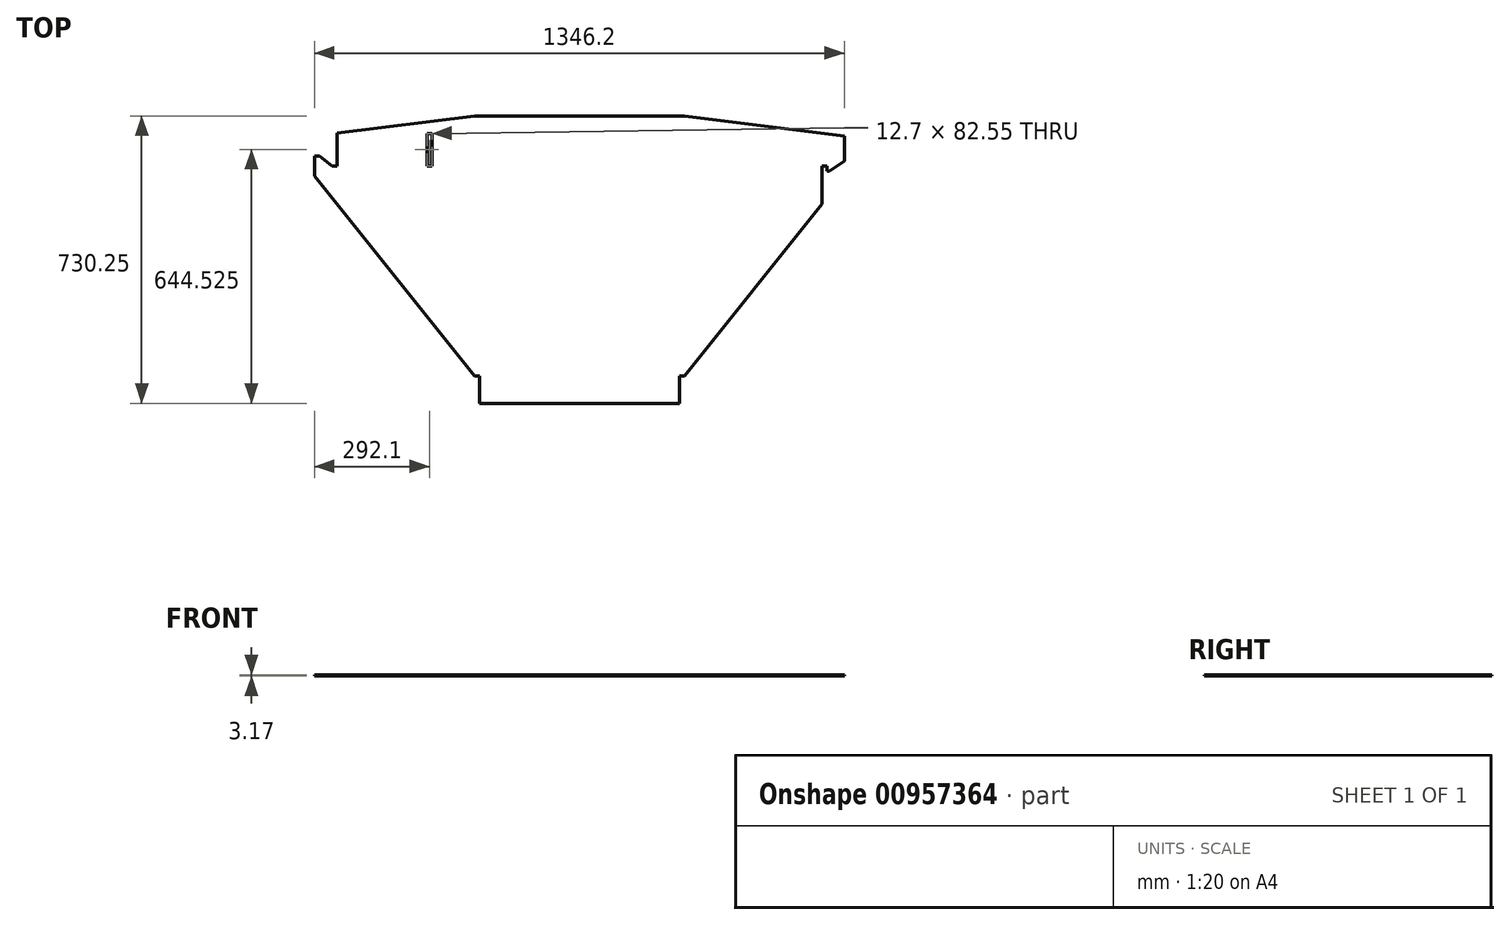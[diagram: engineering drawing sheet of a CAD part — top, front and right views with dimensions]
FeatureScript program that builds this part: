
annotation { "Feature Type Name" : "Feature", "Feature Type Description" : "" }
export const myFeature = defineFeature(function(context is Context, id is Id, definition is map)
    precondition{}
    {
        {
            var Q0;
            Q0=qCreatedBy(makeId("Top.planeOp"),FACE);
            var sketch = newSketch(context, id + "F0", { "sketchPlane" : qUnion([Q0])});
            skLineSegment(sketch, "E0.bottom", {"start": v(0, -660.4) * mm, "end": v(508, -660.4) * mm});
            skLineSegment(sketch, "E0.top", {"start": v(0, 0) * mm, "end": v(508, 0) * mm});
            skLineSegment(sketch, "E0.left", {"start": v(0, -660.4) * mm, "end": v(0, 0) * mm});
            skLineSegment(sketch, "E0.right", {"start": v(508, -660.4) * mm, "end": v(508, 0) * mm});
            skLineSegment(sketch, "E1.bottom", {"start": v(508, -660.4) * mm, "end": v(520.7, -660.4) * mm});
            skLineSegment(sketch, "E1.top", {"start": v(508, 0) * mm, "end": v(520.7, 0) * mm});
            skLineSegment(sketch, "E1.right", {"start": v(520.7, -660.4) * mm, "end": v(520.7, 0) * mm});
            skLineSegment(sketch, "E2", {"start": v(927.1, -50.8) * mm, "end": v(927.1, -114.3) * mm});
            skLineSegment(sketch, "E3", {"start": v(882.65, -139.7) * mm, "end": v(882.65, -127) * mm});
            skLineSegment(sketch, "E4", {"start": v(882.65, -127) * mm, "end": v(869.95, -127) * mm});
            skLineSegment(sketch, "E5", {"start": v(869.95, -127) * mm, "end": v(869.95, -223.84) * mm});
            skLineSegment(sketch, "E6", {"start": v(869.95, -223.84) * mm, "end": v(520.7, -660.4) * mm});
            skLineSegment(sketch, "E7", {"start": v(520.7, 0) * mm, "end": v(927.1, -50.8) * mm});
            skLineSegment(sketch, "E8", {"start": v(869.95, -223.84) * mm, "end": v(927.1, -152.4) * mm, "construction": true});
            skLineSegment(sketch, "E9", {"start": v(882.65, -139.7) * mm, "end": v(889, -139.7) * mm});
            skLineSegment(sketch, "E10", {"start": v(889, -139.7) * mm, "end": v(927.1, -114.3) * mm});
            skLineSegment(sketch, "E11.bottom", {"start": v(0, -660.4) * mm, "end": v(-12.7, -660.4) * mm});
            skLineSegment(sketch, "E11.top", {"start": v(0, 0) * mm, "end": v(-12.7, 0) * mm});
            skLineSegment(sketch, "E11.right", {"start": v(-12.7, -660.4) * mm, "end": v(-12.7, 0) * mm});
            skLineSegment(sketch, "E12", {"start": v(-12.7, -660.4) * mm, "end": v(-419.1, -152.4) * mm});
            skLineSegment(sketch, "E13", {"start": v(-419.1, -152.4) * mm, "end": v(-419.1, -101.6) * mm});
            skLineSegment(sketch, "E14", {"start": v(-419.1, -101.6) * mm, "end": v(-406.4, -101.6) * mm});
            skLineSegment(sketch, "E15", {"start": v(-406.4, -101.6) * mm, "end": v(-374.65, -127) * mm});
            skLineSegment(sketch, "E16", {"start": v(-374.65, -127) * mm, "end": v(-361.95, -127) * mm});
            skLineSegment(sketch, "E17", {"start": v(-361.95, -127) * mm, "end": v(-361.95, -43.66) * mm});
            skLineSegment(sketch, "E18", {"start": v(-361.95, -43.66) * mm, "end": v(-12.7, 0) * mm});
            skLineSegment(sketch, "E19", {"start": v(-361.95, -43.66) * mm, "end": v(-419.1, -50.8) * mm, "construction": true});
            skLineSegment(sketch, "E20.top", {"start": v(0, -730.25) * mm, "end": v(508, -730.25) * mm});
            skLineSegment(sketch, "E20.left", {"start": v(0, -660.4) * mm, "end": v(0, -730.25) * mm});
            skLineSegment(sketch, "E20.right", {"start": v(508, -660.4) * mm, "end": v(508, -730.25) * mm});
            skLineSegment(sketch, "E21.bottom", {"start": v(-133.35, -127) * mm, "end": v(-120.65, -127) * mm});
            skLineSegment(sketch, "E21.top", {"start": v(-133.35, -44.45) * mm, "end": v(-120.65, -44.45) * mm});
            skLineSegment(sketch, "E21.left", {"start": v(-133.35, -127) * mm, "end": v(-133.35, -44.45) * mm});
            skLineSegment(sketch, "E21.right", {"start": v(-120.65, -127) * mm, "end": v(-120.65, -44.45) * mm});
            skSolve(sketch);
        }
        {
            var Q0;
            Q0=makeQuery(id+"F0.imprint","IMPRINT",FACE,{"disambiguationData":[TD([[makeQuery(id+"F0.imprint","IMPRINT",EDGE,{"derivedFrom":sQuery(id+"F0.wireOp",EDGE,"E11.right")}),1.0]])]});
            var Q1;
            Q1=makeQuery(id+"F0.imprint","IMPRINT",FACE,{"disambiguationData":[TD([[makeQuery(id+"F0.imprint","IMPRINT",EDGE,{"derivedFrom":sQuery(id+"F0.wireOp",EDGE,"E0.top")}),-1.0]])]});
            var Q2;
            Q2=makeQuery(id+"F0.imprint","IMPRINT",FACE,{"disambiguationData":[TD([[makeQuery(id+"F0.imprint","IMPRINT",EDGE,{"derivedFrom":sQuery(id+"F0.wireOp",EDGE,"E0.bottom")}),-1.0]])]});
            var Q3;
            Q3=makeQuery(id+"F0.imprint","IMPRINT",FACE,{"disambiguationData":[TD([[makeQuery(id+"F0.imprint","IMPRINT",EDGE,{"derivedFrom":sQuery(id+"F0.wireOp",EDGE,"E1.right")}),-1.0]])]});
            var Q4;
            Q4=makeQuery(id+"F0.imprint","IMPRINT",FACE,{"disambiguationData":[TD([[makeQuery(id+"F0.imprint","IMPRINT",EDGE,{"derivedFrom":sQuery(id+"F0.wireOp",EDGE,"E1.bottom")}),1.0]])]});
            var Q5;
            Q5=makeQuery(id+"F0.imprint","IMPRINT",FACE,{"disambiguationData":[TD([[makeQuery(id+"F0.imprint","IMPRINT",EDGE,{"derivedFrom":sQuery(id+"F0.wireOp",EDGE,"E11.bottom")}),-1.0]])]});
            extrude(context, id + "F1", {"entities" : qUnion([Q0, Q1, Q2, Q3, Q4, Q5]), "depth" : 3.17 * mm, "offsetDistance" : 25.4 * mm});
        }
    });
